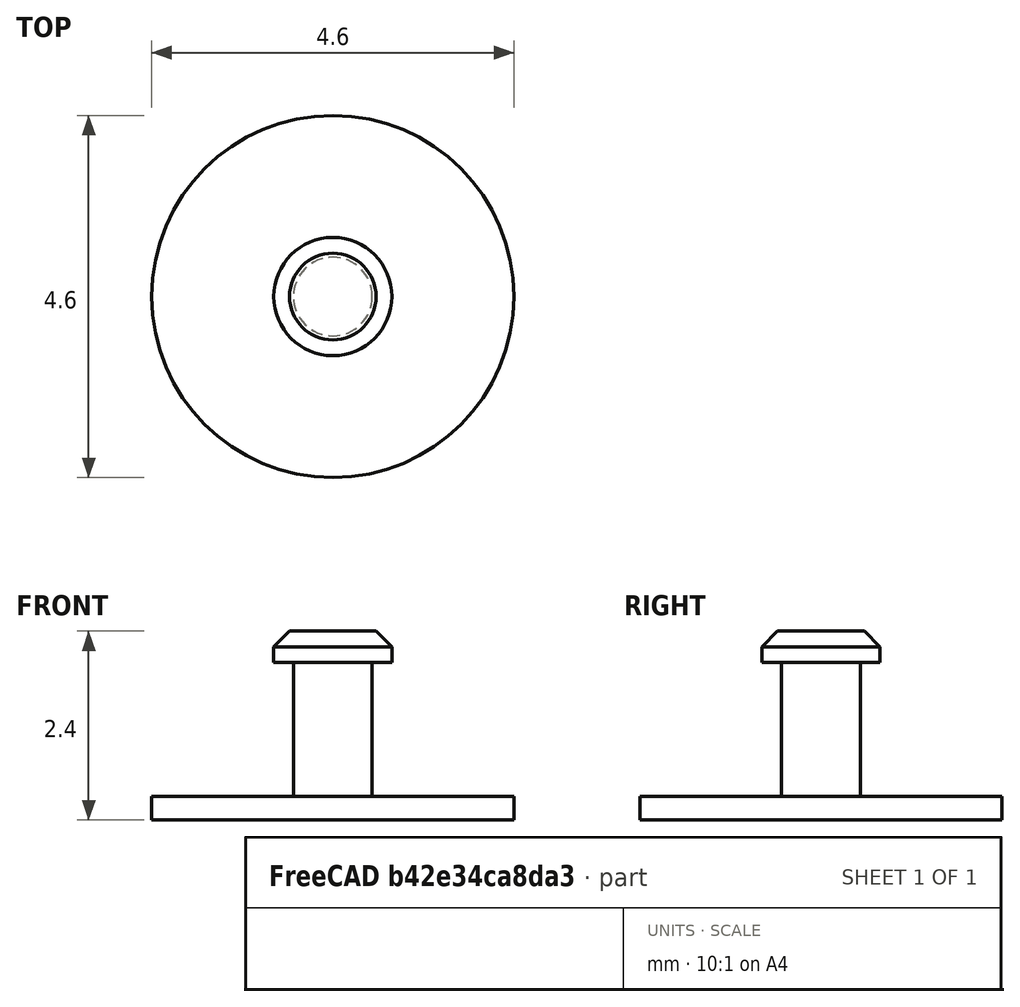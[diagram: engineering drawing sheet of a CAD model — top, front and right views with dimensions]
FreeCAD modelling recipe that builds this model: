
FCSTD DOCUMENT  (FreeCAD 0.19R)
Label: band-pin
License: All rights reserved
LicenseURL: http://en.wikipedia.org/wiki/All_rights_reserved
objects: PartDesign::AdditiveCylinder×3, PartDesign::Chamfer×1, PartDesign::Body×1
note: 8 computed .brp shape members not serialized (recipe doc carries the construction recipe); baked Part::Feature solids carry a one-line shape summary decoded from their .brp

FEATURE [PartDesign::AdditiveCylinder] Cylinder  label="base"
  Angle = 360
  AttacherType = Attacher::AttachEngine3D
  Height = 0.3
  MapMode = 5
  Radius = 2.3
  Support = -> [XY_Plane]
FEATURE [PartDesign::AdditiveCylinder] Cylinder001  label="pin-to-hole"
  Angle = 360
  AttacherType = Attacher::AttachEngine3D
  BaseFeature = -> Cylinder
  Height = 2
  Radius = 0.5
FEATURE [PartDesign::AdditiveCylinder] Cylinder002  label="pin-top"
  Angle = 360
  AttacherType = Attacher::AttachEngine3D
  BaseFeature = -> Cylinder001
  Height = 0.4
  MapMode = 5
  Placement = pos=(0,0,2) rot=(0,0,1;0rad)
  Radius = 0.75
  Support = -> [Cylinder001]
FEATURE [PartDesign::Chamfer] Chamfer  label="pin-chamfer"
  Base = -> Cylinder002 [Edge1]
  BaseFeature = -> Cylinder002
  Placement = pos=(0,0,2) rot=(0,0,1;0rad)
  Size = 0.2
FEATURE [PartDesign::Body] Body
  Group = -> [Cylinder,Cylinder001,Cylinder002,Chamfer]
  Origin = -> Origin
  Tip = -> Chamfer
